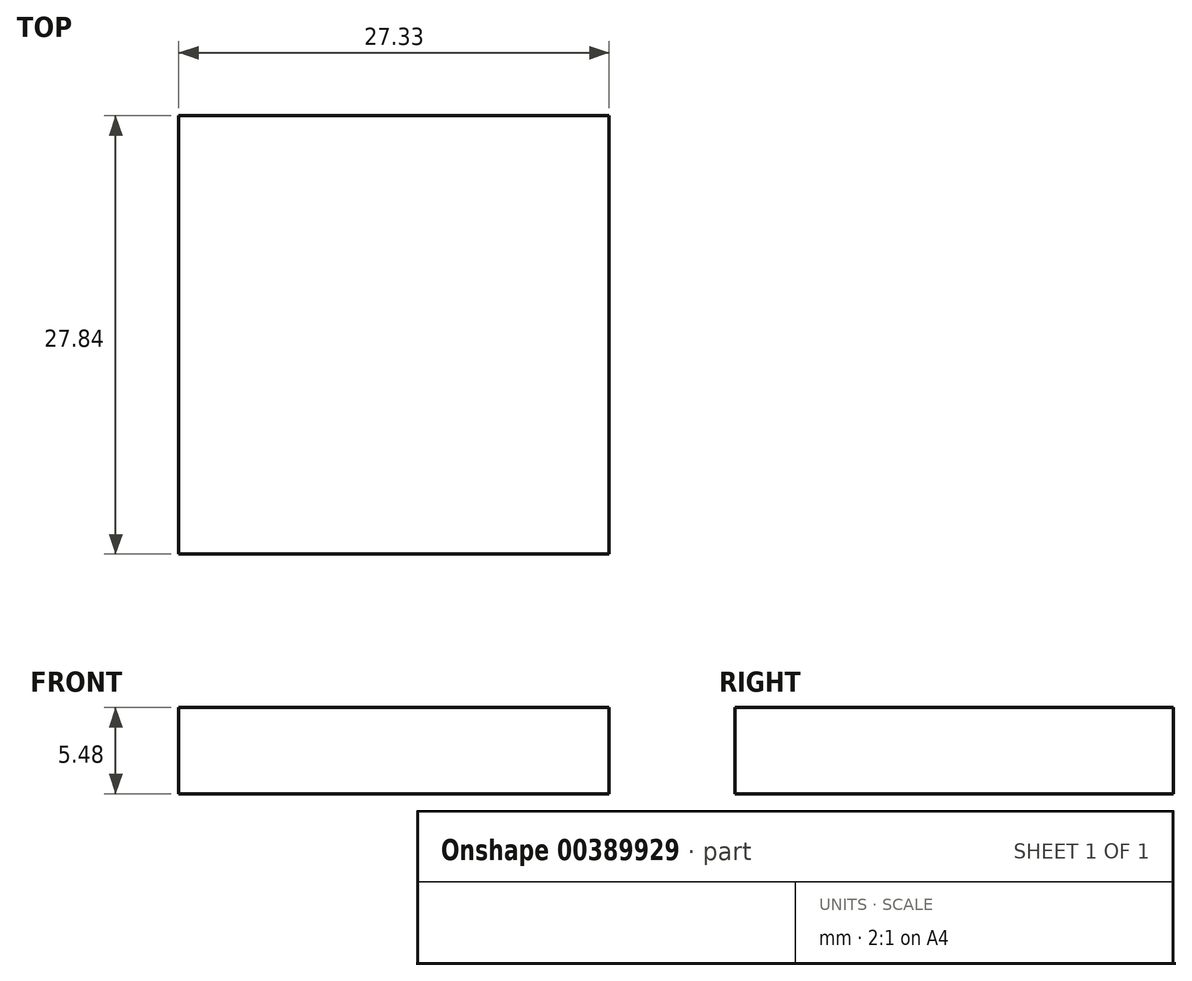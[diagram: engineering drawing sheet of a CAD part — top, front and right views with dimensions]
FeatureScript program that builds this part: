
annotation { "Feature Type Name" : "Feature", "Feature Type Description" : "" }
export const myFeature = defineFeature(function(context is Context, id is Id, definition is map)
    precondition{}
    {
        {
            var Q0;
            Q0=qCreatedBy(makeId("Top.planeOp"),FACE);
            var sketch = newSketch(context, id + "F0", { "sketchPlane" : qUnion([Q0])});
            skLineSegment(sketch, "E0.bottom", {"start": v(0, 37.69) * mm, "end": v(-27.33, 37.69) * mm});
            skLineSegment(sketch, "E0.top", {"start": v(0, 9.85) * mm, "end": v(-27.33, 9.85) * mm});
            skLineSegment(sketch, "E0.left", {"start": v(0, 37.69) * mm, "end": v(0, 9.85) * mm});
            skLineSegment(sketch, "E0.right", {"start": v(-27.33, 37.69) * mm, "end": v(-27.33, 9.85) * mm});
            skSolve(sketch);
        }
        {
            var Q0;
            Q0 = qSketchRegion(id + "F0", true);
            extrude(context, id + "F1", {"entities" : qUnion([Q0]), "depth" : 5.48 * mm});
        }
    });
